# Revit family: Bottle_Filler-Oasis-Aqua_Pointe_Sports_Bottle_Filler-MWEBF
name_source: partatom
category: Plumbing Fixtures
revit_build: Autodesk Revit Architecture 2013 (Build: 20130531_2115(x64)
units: mm (PartAtom-declared; Revit-internal decimal feet)

## types (1)
- MWEBF
    Apparent Load = 7 VA
    Base Rate = 0 GPM
    CW Connection = No
    CWFU = 0
    Chiller = No
    Cold Water Diameter = 0"
    Cold Water Radius = 0"
    Compression HP = 0 VA
    Default Elevation = 2' - 4 3/8"
    Description = Aqua Pointe Sports Bottle Filler
    Display Panel = Screen – Oasis- LCD Display
    Finish = Metal - Oasis International - Brushed Stainless Steel - Exterior Finish
    Full Load Amps = 0 A
    Manufacturer = Oasis International
    Manufacturer Fax Number = (614)322-4557
    Metal Finish = Metal - Oasis International - Brushed Stainless Steel - Exterior Finish
    Model = MWEBF
    Number of Poles = 1
    Power Factor = 1
    Product Documentation Link = http://www.oasiscoolers.com
    Product Name = Non Refrigerated Electronic Bottle Filler
    Product Page URL = http://www.oasiscoolers.com
    Rated Capacity = 0 GPM
    Rated Watts = 7 W
    Sanitary Diameter = 1"
    Sanitary Radius = 1"
    URL = http://www.oasiscoolers.com
    Voltage = 115 V
    WFU = 0
    Width = 3' - 2 3/4"

## geometry (parser evidence)
native form markers: Blend x8, Sweep x7
no freeform markers — native parametric forms only
